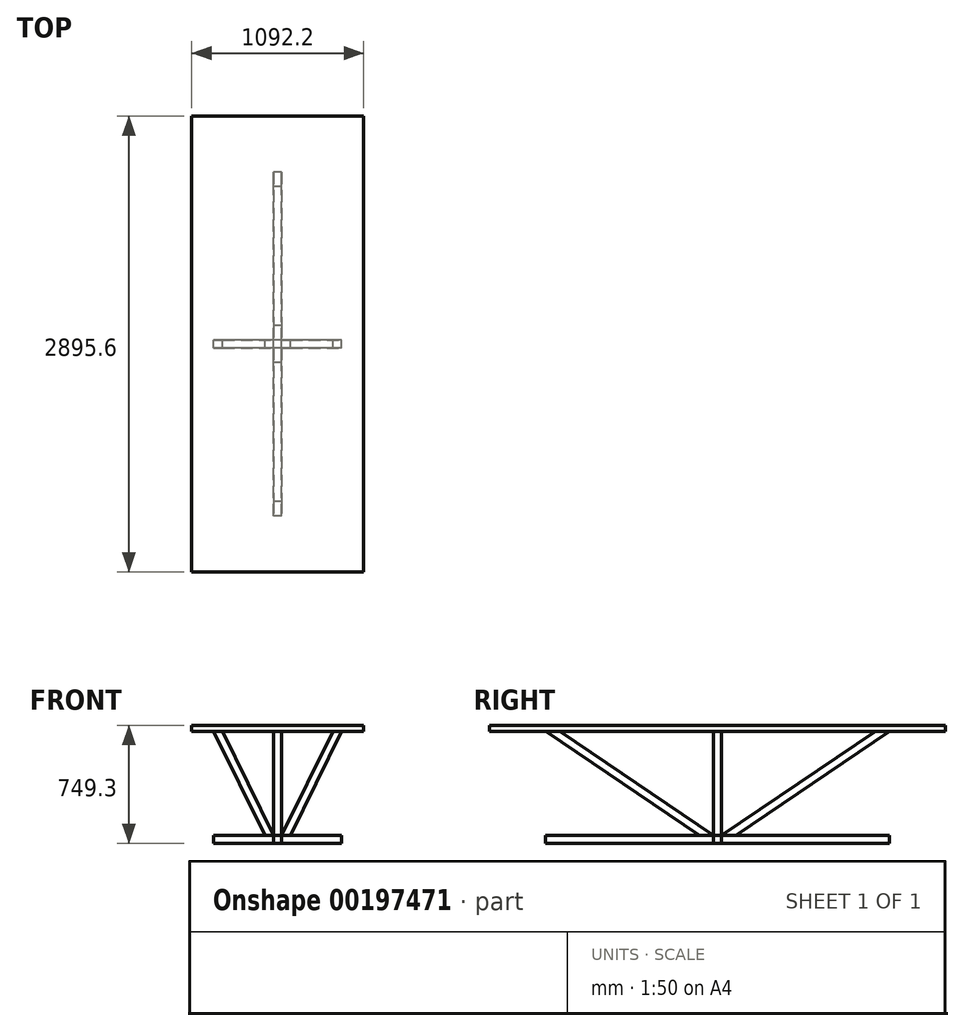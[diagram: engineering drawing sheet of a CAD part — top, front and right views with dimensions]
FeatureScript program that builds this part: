
annotation { "Feature Type Name" : "Feature", "Feature Type Description" : "" }
export const myFeature = defineFeature(function(context is Context, id is Id, definition is map)
    precondition{}
    {
        {
            var Q0;
            Q0=qCreatedBy(makeId("Right.planeOp"),FACE);
            var sketch = newSketch(context, id + "F0", { "sketchPlane" : qUnion([Q0])});
            skLineSegment(sketch, "E0.bottom", {"start": v(-1092.2, 25.4) * mm, "end": v(1092.2, 25.4) * mm});
            skLineSegment(sketch, "E0.top", {"start": v(-1092.2, -25.4) * mm, "end": v(1092.2, -25.4) * mm});
            skLineSegment(sketch, "E0.left", {"start": v(-1092.2, 25.4) * mm, "end": v(-1092.2, -25.4) * mm});
            skLineSegment(sketch, "E0.right", {"start": v(1092.2, 25.4) * mm, "end": v(1092.2, -25.4) * mm});
            skPoint(sketch, "E0.middle", {"position": v(0, 0) * mm});
            skSolve(sketch);
        }
        {
            var Q0;
            Q0=makeQuery(id+"F0.imprint","IMPRINT",FACE,{"disambiguationData":[TD([[makeQuery(id+"F0.imprint","IMPRINT",EDGE,{"derivedFrom":sQuery(id+"F0.wireOp",EDGE,"E0.bottom")}),-1.0]])]});
            extrude(context, id + "F1", {"entities" : qUnion([Q0]), "endBound" : BoundingType.SYMMETRIC, "depth" : 50.8 * mm});
        }
        {
            var Q0;
            Q0=qCreatedBy(makeId("Right.planeOp"),FACE);
            var sketch = newSketch(context, id + "F2", { "sketchPlane" : qUnion([Q0])});
            skLineSegment(sketch, "E1.bottom", {"start": v(25.4, -25.4) * mm, "end": v(-25.4, -25.4) * mm});
            skLineSegment(sketch, "E1.top", {"start": v(25.4, 25.4) * mm, "end": v(-25.4, 25.4) * mm});
            skLineSegment(sketch, "E1.left", {"start": v(25.4, -25.4) * mm, "end": v(25.4, 25.4) * mm});
            skLineSegment(sketch, "E1.right", {"start": v(-25.4, -25.4) * mm, "end": v(-25.4, 25.4) * mm});
            skPoint(sketch, "E1.middle", {"position": v(0, 0) * mm});
            skSolve(sketch);
        }
        {
            var Q0;
            Q0 = qSketchRegion(id + "F2", true);
            extrude(context, id + "F3", {"entities" : qUnion([Q0]), "operationType" : NewBodyOperationType.ADD, "endBound" : BoundingType.SYMMETRIC, "depth" : 812.8 * mm});
        }
        {
            var Q0;
            Q0=qCreatedBy(makeId("Right.planeOp"),FACE);
            var sketch = newSketch(context, id + "F4", { "sketchPlane" : qUnion([Q0])});
            skLineSegment(sketch, "E2", {"start": v(0, -25.4) * mm, "end": v(0, 685.8) * mm});
            skLineSegment(sketch, "E3.bottom", {"start": v(0, 685.8) * mm, "end": v(1447.8, 685.8) * mm});
            skLineSegment(sketch, "E3.top", {"start": v(0, 723.9) * mm, "end": v(1447.8, 723.9) * mm});
            skLineSegment(sketch, "E3.left", {"start": v(0, 685.8) * mm, "end": v(0, 723.9) * mm});
            skLineSegment(sketch, "E3.right", {"start": v(1447.8, 685.8) * mm, "end": v(1447.8, 723.9) * mm});
            skLineSegment(sketch, "E4.MirrorCS", {"start": v(0, 762) * mm, "end": v(1447.8, 762) * mm});
            skLineSegment(sketch, "E5.MirrorCS", {"start": v(0, 762) * mm, "end": v(0, 723.9) * mm});
            skLineSegment(sketch, "E6.MirrorCS", {"start": v(-1447.8, 685.8) * mm, "end": v(-1447.8, 723.9) * mm});
            skLineSegment(sketch, "E7.MirrorCS", {"start": v(0, 762) * mm, "end": v(-1447.8, 762) * mm});
            skLineSegment(sketch, "E8.MirrorCS", {"start": v(0, 723.9) * mm, "end": v(-1447.8, 723.9) * mm});
            skLineSegment(sketch, "E9.MirrorCS", {"start": v(0, 685.8) * mm, "end": v(-1447.8, 685.8) * mm});
            skSolve(sketch);
        }
        {
            var Q0;
            Q0=makeQuery(id+"F4.imprint","IMPRINT",FACE,{"disambiguationData":[TD([[makeQuery(id+"F4.imprint","IMPRINT",EDGE,{"derivedFrom":sQuery(id+"F4.wireOp",EDGE,"E3.left")}),1.0]])]});
            var Q1;
            Q1=makeQuery(id+"F4.imprint","IMPRINT",FACE,{"disambiguationData":[TD([[makeQuery(id+"F4.imprint","IMPRINT",EDGE,{"derivedFrom":sQuery(id+"F4.wireOp",EDGE,"E3.bottom")}),1.0]])]});
            extrude(context, id + "F5", {"entities" : qUnion([Q0, Q1]), "endBound" : BoundingType.SYMMETRIC, "depth" : 1092.2 * mm});
        }
        {
            var Q0;
            Q0=qCreatedBy(makeId("Right.planeOp"),FACE);
            var sketch = newSketch(context, id + "F6", { "sketchPlane" : qUnion([Q0])});
            skLineSegment(sketch, "E10", {"start": v(25.4, 25.4) * mm, "end": v(1001.57, 686.13) * mm});
            skLineSegment(sketch, "E11", {"start": v(1001.57, 686.13) * mm, "end": v(1092.2, 686.13) * mm});
            skLineSegment(sketch, "E12", {"start": v(1092.2, 686.13) * mm, "end": v(116.03, 25.4) * mm});
            skLineSegment(sketch, "E13", {"start": v(116.03, 25.4) * mm, "end": v(25.4, 25.4) * mm});
            skLineSegment(sketch, "E14", {"start": v(0, 686.13) * mm, "end": v(1092.2, 686.13) * mm});
            skLineSegment(sketch, "E15", {"start": v(1092.2, 686.13) * mm, "end": v(1092.2, 25.4) * mm});
            skSolve(sketch);
        }
        {
            var Q0;
            {var subQ0=sQuery(id+"F6.wireOp",EDGE,"E10");Q0=makeQuery(id+"F6.imprint","IMPRINT",FACE,{"disambiguationData":[TD([[makeQuery(id+"F6.imprint","IMPRINT",EDGE,{"derivedFrom":subQ0}),-1.0]])]});}
            extrude(context, id + "F7", {"entities" : qUnion([Q0]), "endBound" : BoundingType.SYMMETRIC, "depth" : 50.8 * mm});
        }
        {
            var Q0;
            Q0=makeQuery(id+"F7.opExtrude","SWEPT_BODY",BODY,{"disambiguationData":[OSD([sQuery(id+"F6.wireOp",EDGE,"E10"),sQuery(id+"F6.wireOp",EDGE,"E12"),sQuery(id+"F6.wireOp",EDGE,"E13"),sQuery(id+"F6.wireOp",EDGE,"E14")])]});
            var Q1;
            Q1=qCreatedBy(makeId("Front.planeOp"),FACE);
            mirror(context, id + "F8", {"entities" : qUnion([Q0]), "mirrorPlane" : qUnion([Q1])});
        }
        {
            var Q0;
            Q0=qCreatedBy(makeId("Front.planeOp"),FACE);
            var sketch = newSketch(context, id + "F9", { "sketchPlane" : qUnion([Q0])});
            skLineSegment(sketch, "E16", {"start": v(-25.4, 25.4) * mm, "end": v(-82, 25.4) * mm});
            skLineSegment(sketch, "E17", {"start": v(-82, 25.4) * mm, "end": v(-406.4, 685.87) * mm});
            skLineSegment(sketch, "E18", {"start": v(-406.4, 685.87) * mm, "end": v(-349.8, 685.87) * mm});
            skLineSegment(sketch, "E19", {"start": v(-349.8, 685.87) * mm, "end": v(-25.4, 25.4) * mm});
            skLineSegment(sketch, "E20", {"start": v(0, 685.87) * mm, "end": v(-406.4, 685.87) * mm});
            skLineSegment(sketch, "E21", {"start": v(-406.4, 685.87) * mm, "end": v(-406.4, 25.4) * mm});
            skSolve(sketch);
        }
        {
            var Q0;
            Q0=makeQuery(id+"F9.imprint","IMPRINT",FACE,{"disambiguationData":[TD([[makeQuery(id+"F9.imprint","IMPRINT",EDGE,{"derivedFrom":sQuery(id+"F9.wireOp",EDGE,"E16")}),-1.0]])]});
            extrude(context, id + "F10", {"entities" : qUnion([Q0]), "endBound" : BoundingType.SYMMETRIC, "depth" : 50.8 * mm});
        }
        {
            var Q0;
            Q0=makeQuery(id+"F10.opExtrude","SWEPT_BODY",BODY,{"disambiguationData":[OSD([sQuery(id+"F9.wireOp",EDGE,"E16"),sQuery(id+"F9.wireOp",EDGE,"E17"),sQuery(id+"F9.wireOp",EDGE,"E19"),sQuery(id+"F9.wireOp",EDGE,"E20")])]});
            var Q1;
            Q1=qCreatedBy(makeId("Right.planeOp"),FACE);
            mirror(context, id + "F11", {"entities" : qUnion([Q0]), "mirrorPlane" : qUnion([Q1])});
        }
    });
